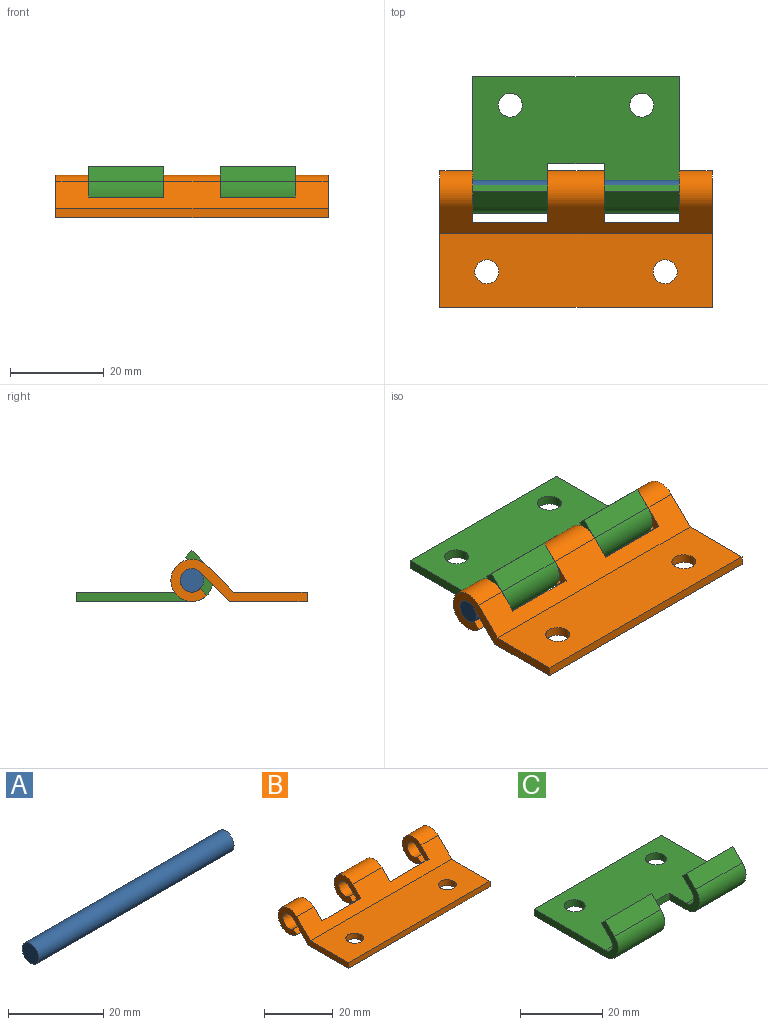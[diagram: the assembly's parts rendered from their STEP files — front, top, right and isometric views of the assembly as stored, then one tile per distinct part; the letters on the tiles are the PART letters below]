
ASSEMBLY  parts=3 mates=3
PART A: 3 faces, bbox 58x5x5 mm
  f0: cylinder r=2.5mm len=58mm, axis (-1,0,0), area 911.1mm2, adj f1,f2
  f1: plane 5x5mm, normal (1,0,0), area 19.6mm2, adj f0
  f2: plane 5x5mm, normal (-1,0,0), area 19.6mm2, adj f0
PART B: 24 faces, bbox 58x29x9 mm
  f0: cylinder r=2.5mm len=12mm, axis (-1,0,0), area 141.4mm2, adj f2,f10,f13,f21
  f1: cylinder r=4.5mm len=12mm, axis (-1,0,0), area 254.5mm2, adj f6,f10,f13,f21
  f2: plane 58x6.27mm, normal (0,0.71,-0.71), area 300mm2, adj f0,f3,f9,f11,f12,f13,f14,f16
  f3: cylinder r=2.5mm len=7mm, axis (-1,0,0), area 82.5mm2, adj f2,f4,f11,f14
  f4: plane 7x1.41mm, normal (0,-0.71,0.71), area 14mm2, adj f3,f5,f11,f14
  f5: cylinder r=4.5mm len=9mm, axis (-1,0,0), area 148.4mm2, adj f4,f6,f11,f14
  f6: plane 58x5.68mm, normal (0,-0.71,0.71), area 315.9mm2, adj f1,f5,f7,f11,f12,f13,f14,f18
  f7: plane 58x15.64mm, normal (0,0,1), area 866mm2, adj f6,f8,f11,f15,f19,f23
  f8: plane 58x2mm, normal (0,-1,0), area 116mm2, adj f7,f9,f11,f19
  f9: plane 58x16.46mm, normal (0,0,-1), area 914.1mm2, adj f2,f8,f11,f15,f19,f23
  f10: plane 12x1.41mm, normal (0,-0.71,0.71), area 24mm2, adj f0,f1,f13,f21
  f11: plane 29x9mm, normal (1,0,0), area 82mm2, adj f2,f3,f4,f5,f6,f7,f8,f9
  f12: plane 16x2.83mm, normal (0,1,0), area 45.3mm2, adj f2,f6,f13,f14
  f13: plane 11x9mm, normal (1,0,0), area 44.4mm2, adj f0,f1,f2,f6,f10,f12
  f14: plane 11x9mm, normal (-1,0,0), area 44.4mm2, adj f2,f3,f4,f5,f6,f12
  f15: cylinder r=2.55mm len=5.1mm, axis (0,0,1), area 32mm2, adj f7,f9
  f16: cylinder r=2.5mm len=7mm, axis (1,0,0), area 82.5mm2, adj f2,f17,f19,f22
  f17: plane 7x1.41mm, normal (0,-0.71,0.71), area 14mm2, adj f16,f18,f19,f22
  f18: cylinder r=4.5mm len=9mm, axis (1,0,0), area 148.4mm2, adj f6,f17,f19,f22
  f19: plane 29x9mm, normal (-1,0,0), area 82mm2, adj f2,f6,f7,f8,f9,f16,f17,f18
  f20: plane 16x2.83mm, normal (0,1,0), area 45.3mm2, adj f2,f6,f21,f22
  f21: plane 11x9mm, normal (-1,0,0), area 44.4mm2, adj f0,f1,f2,f6,f10,f20
  f22: plane 11x9mm, normal (1,0,0), area 44.4mm2, adj f2,f6,f16,f17,f18,f20
  f23: cylinder r=2.55mm len=5.1mm, axis (0,0,1), area 32mm2, adj f7,f9
PART C: 20 faces, bbox 44x29x10.9 mm
  f0: plane 44x24.5mm, normal (0,0,1), area 965.1mm2, adj f1,f4,f8,f9,f10,f11,f12,f17
  f1: cylinder r=2.5mm len=16mm, axis (-1,0,0), area 94.2mm2, adj f0,f5,f8,f9
  f2: cylinder r=4.5mm len=16mm, axis (-1,0,0), area 169.6mm2, adj f3,f7,f8,f9
  f3: plane 44x24.5mm, normal (0,0,-1), area 965.1mm2, adj f2,f4,f8,f9,f10,f11,f13,f17
  f4: plane 44x2mm, normal (0,1,0), area 88mm2, adj f0,f3,f8,f17
  f5: plane 16x3.18mm, normal (0,0.71,-0.71), area 72mm2, adj f1,f6,f8,f9
  f6: plane 16x1.41mm, normal (0,0.71,0.71), area 32mm2, adj f5,f7,f8,f9
  f7: plane 16x3.18mm, normal (0,-0.71,0.71), area 72mm2, adj f2,f6,f8,f9
  f8: plane 29x10.86mm, normal (1,0,0), area 74.5mm2, adj f0,f1,f2,f3,f4,f5,f6,f7
  f9: plane 10.86x10.5mm, normal (-1,0,0), area 37.5mm2, adj f0,f1,f2,f3,f5,f6,f7,f10
  f10: plane 12x2mm, normal (0,-1,0), area 24mm2, adj f0,f3,f9,f18
  f11: cylinder r=2.55mm len=5.1mm, axis (0,0,1), area 32mm2, adj f0,f3
  f12: cylinder r=2.5mm len=16mm, axis (1,0,0), area 94.2mm2, adj f0,f14,f17,f18
  f13: cylinder r=4.5mm len=16mm, axis (1,0,0), area 169.6mm2, adj f3,f16,f17,f18
  f14: plane 16x3.18mm, normal (0,0.71,-0.71), area 72mm2, adj f12,f15,f17,f18
  f15: plane 16x1.41mm, normal (0,0.71,0.71), area 32mm2, adj f14,f16,f17,f18
  f16: plane 16x3.18mm, normal (0,-0.71,0.71), area 72mm2, adj f13,f15,f17,f18
  f17: plane 29x10.86mm, normal (-1,0,0), area 74.5mm2, adj f0,f3,f4,f12,f13,f14,f15,f16
  f18: plane 10.86x10.5mm, normal (1,0,0), area 37.5mm2, adj f0,f3,f10,f12,f13,f14,f15,f16
  f19: cylinder r=2.55mm len=5.1mm, axis (0,0,1), area 32mm2, adj f0,f3
PLACE A rot(axis=(0,0.83,-0.56),180deg) t=(0,0,4.5)mm
PLACE B t=(0,0,4.5)mm fixed
PLACE C rot(axis=(1,0,0),0deg) t=(0,0,4.5)mm
MATE cylindrical A.f0 <-> B.f0  axis (1,0,0) through (0,0,4.5)mm
MATE cylindrical A.f0 <-> C.f1  axis (1,0,0) through (0,0,4.5)mm
MATE revolute B.f0 <-> C.f1  axis (-1,0,0) through (0,0,4.5)mm
